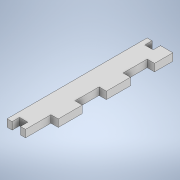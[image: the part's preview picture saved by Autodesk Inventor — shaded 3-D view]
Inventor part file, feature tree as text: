
AUTODESK INVENTOR PART (.ipt)
format: ipt  version: 2020 (Build 240168000, 168)  size: 125,440 bytes
history: native  units: mm
features: extrude x1, sketch x1
ambient origin geometry x8: Origin, YZ Plane, XZ Plane, XY Plane, X Axis, Y Axis, Z Axis, Center Point
bodies: Solide1 (feature_tree)
feature tree (2):
  extrude  "Extrusion1"  Depth=419.0mm
  sketch  "Esquisse1"
